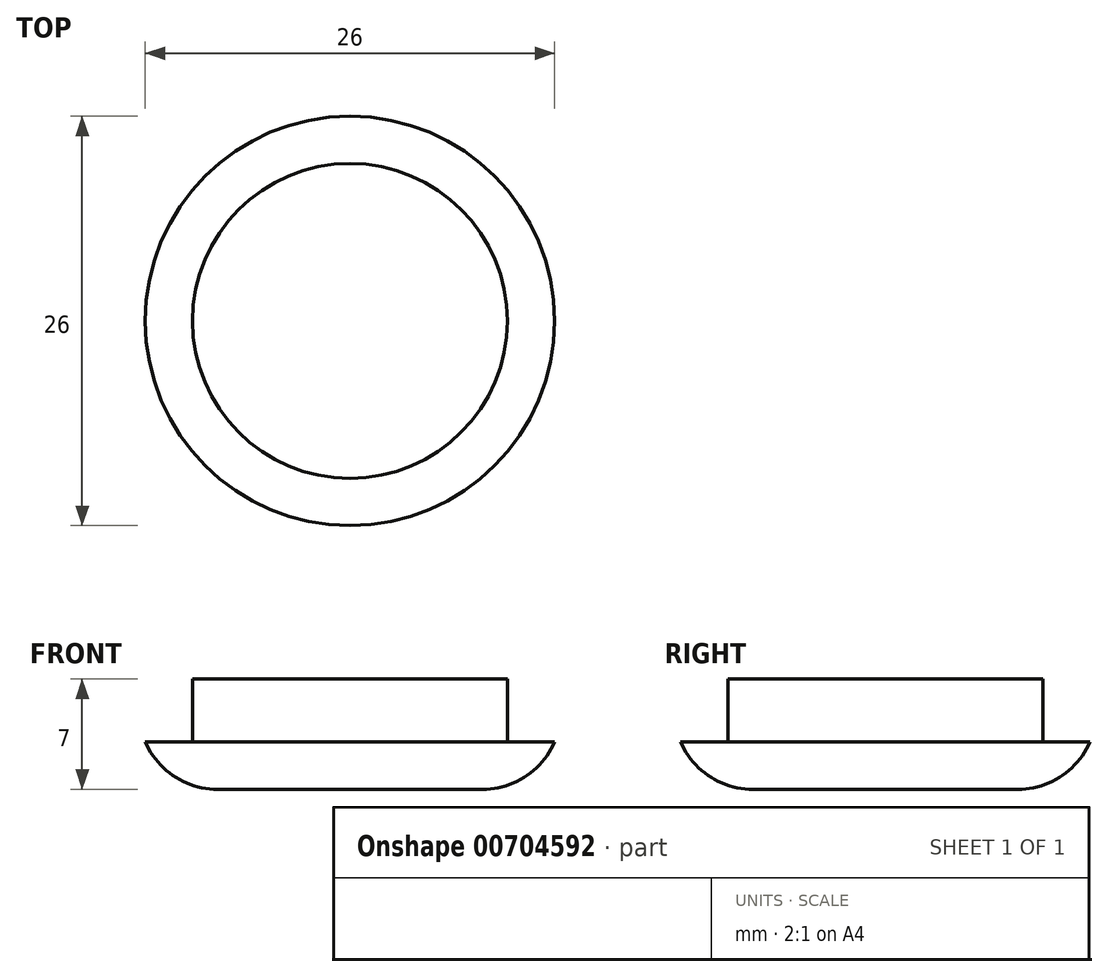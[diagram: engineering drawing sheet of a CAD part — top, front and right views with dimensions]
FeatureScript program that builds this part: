
annotation { "Feature Type Name" : "Feature", "Feature Type Description" : "" }
export const myFeature = defineFeature(function(context is Context, id is Id, definition is map)
    precondition{}
    {
        {
            var Q0;
            Q0=qCreatedBy(makeId("Top.planeOp"),FACE);
            var sketch = newSketch(context, id + "F0", { "sketchPlane" : qUnion([Q0])});
            skCircle(sketch, "E0", {"center": v(0, 0) * mm, "radius": 13 * mm});
            skSolve(sketch);
        }
        {
            var Q0;
            Q0=qCreatedBy(makeId("Top.planeOp"),FACE);
            var sketch = newSketch(context, id + "F1", { "sketchPlane" : qUnion([Q0])});
            skCircle(sketch, "E1", {"center": v(0, 0) * mm, "radius": 10 * mm});
            skSolve(sketch);
        }
        {
            var Q0;
            Q0=makeQuery(id+"F1.imprint","IMPRINT",FACE,{"disambiguationData":[TD([[makeQuery(id+"F1.imprint","IMPRINT",EDGE,{"derivedFrom":sQuery(id+"F1.wireOp",EDGE,"E1")}),1.0]])]});
            extrude(context, id + "F2", {"entities" : qUnion([Q0]), "depth" : 7 * mm, "offsetDistance" : 25 * mm});
        }
        {
            var Q0;
            Q0=makeQuery(id+"F0.imprint","IMPRINT",FACE,{"disambiguationData":[TD([[makeQuery(id+"F0.imprint","IMPRINT",EDGE,{"derivedFrom":sQuery(id+"F0.wireOp",EDGE,"E0")}),1.0]])]});
            extrude(context, id + "F3", {"entities" : qUnion([Q0]), "operationType" : NewBodyOperationType.ADD, "depth" : 3 * mm, "offsetDistance" : 25 * mm});
        }
        {
            var Q0;
            Q0=makeQuery(id+"F3.opExtrude","CAP_EDGE",EDGE,{"disambiguationData":[OSD([sQuery(id+"F0.wireOp",EDGE,"E0")])],"isStart":true});
            fillet(context, id + "F4", {"entities" : qUnion([Q0]), "radius" : 5 * mm, "tangentPropagation" : true, "allowEdgeOverflow" : false});
        }
    });
